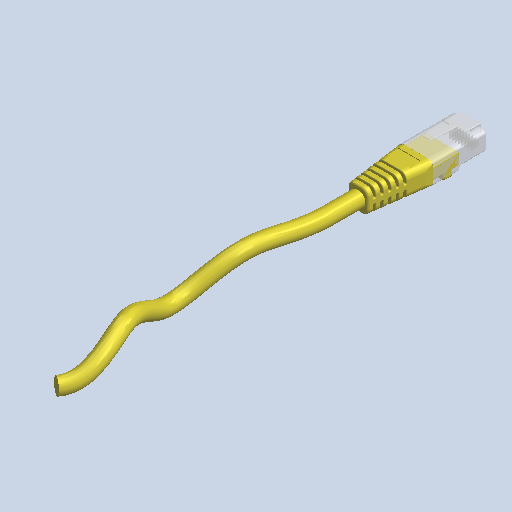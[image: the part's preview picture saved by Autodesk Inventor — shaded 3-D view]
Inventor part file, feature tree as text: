
AUTODESK INVENTOR PART (.ipt)
format: ipt  version: 2022.1 (Build 261234000, 234)  size: 702,976 bytes
history: mixed  units: mm (DEFAULTED — no unit token found)
features: other x10, sweep x1, imported_body x1
bodies: Body1 (imported_parasolid), Body2 (imported_parasolid)
feature tree (12):
  other  "Sólido1"
  other  "Origen"
  other  "Plano YZ"
  other  "Plano XZ"
  other  "Plano XY"
  other  "Eje X"
  other  "Eje Y"
  other  "Eje Z"
  other  "Sólido2"
  other  "Cut-Extrude7"
  sweep  "Sweep1"
  imported_body  NMx_Import_Brep_tag  [imported B-rep: ~10 faces, bbox_mm=None]
